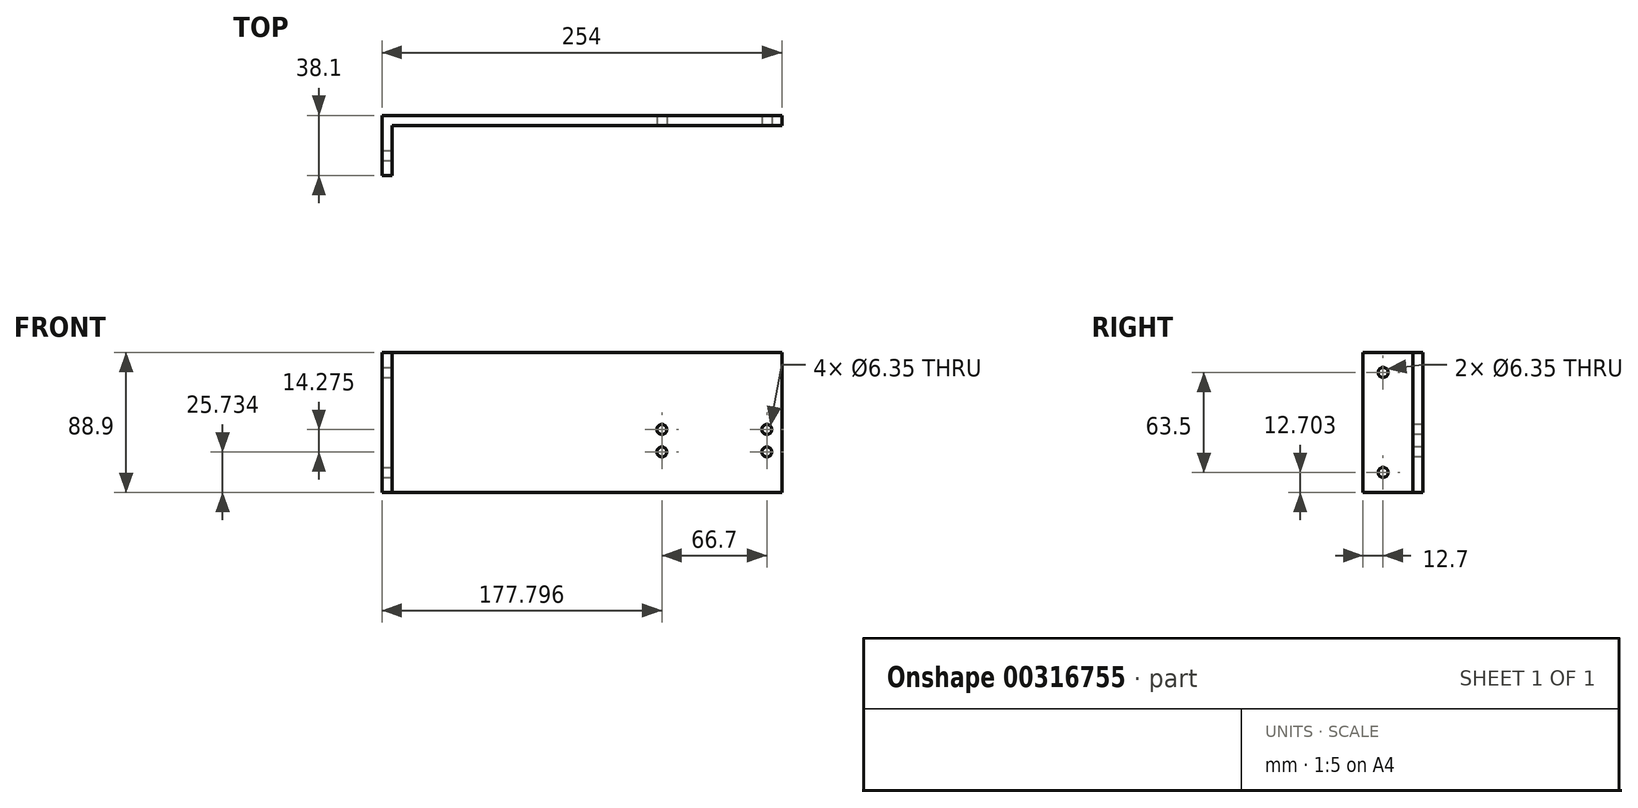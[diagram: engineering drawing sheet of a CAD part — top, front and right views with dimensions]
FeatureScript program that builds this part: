
annotation { "Feature Type Name" : "Feature", "Feature Type Description" : "" }
export const myFeature = defineFeature(function(context is Context, id is Id, definition is map)
    precondition{}
    {
        {
            var Q0;
            Q0=qCreatedBy(makeId("Front.planeOp"),FACE);
            var sketch = newSketch(context, id + "F0", { "sketchPlane" : qUnion([Q0])});
            skLineSegment(sketch, "E0.bottom", {"start": v(-29.12, 31.27) * mm, "end": v(224.88, 31.27) * mm});
            skLineSegment(sketch, "E0.top", {"start": v(-29.12, -57.63) * mm, "end": v(224.88, -57.63) * mm});
            skLineSegment(sketch, "E0.left", {"start": v(-29.12, 31.27) * mm, "end": v(-29.12, -57.63) * mm});
            skLineSegment(sketch, "E0.right", {"start": v(224.88, 31.27) * mm, "end": v(224.88, -57.63) * mm});
            skSolve(sketch);
        }
        {
            var Q0;
            Q0=makeQuery(id+"F0.imprint","IMPRINT",FACE,{"disambiguationData":[TD([[makeQuery(id+"F0.imprint","IMPRINT",EDGE,{"derivedFrom":sQuery(id+"F0.wireOp",EDGE,"E0.bottom")}),-1.0]])]});
            extrude(context, id + "F1", {"entities" : qUnion([Q0]), "depth" : 6.35 * mm});
        }
        {
            var Q0;
            Q0=makeQuery(id+"F1.opExtrude","CAP_FACE",FACE,{"disambiguationData":[OSD([sQuery(id+"F0.wireOp",EDGE,"E0.bottom"),sQuery(id+"F0.wireOp",EDGE,"E0.top"),sQuery(id+"F0.wireOp",EDGE,"E0.left"),sQuery(id+"F0.wireOp",EDGE,"E0.right")])],"isStart":false});
            var sketch = newSketch(context, id + "F2", { "sketchPlane" : qUnion([Q0])});
            skPoint(sketch, "E1", {"position": v(148.68, -31.9) * mm});
            skPoint(sketch, "E2", {"position": v(148.68, -17.62) * mm});
            skPoint(sketch, "E3", {"position": v(215.38, -17.62) * mm});
            skPoint(sketch, "E4", {"position": v(215.38, -31.9) * mm});
            skSolve(sketch);
        }
        {
            var Q0;
            Q0=sQuery(id+"F2.wireOp",VERTEX,"E2");
            var Q1;
            Q1=sQuery(id+"F2.wireOp",VERTEX,"E3");
            var Q2;
            Q2=sQuery(id+"F2.wireOp",VERTEX,"E4");
            var Q3;
            Q3=sQuery(id+"F2.wireOp",VERTEX,"E1");
            var Q4;
            Q4=makeQuery(id+"F1.opExtrude","SWEPT_BODY",BODY,{"disambiguationData":[OSD([sQuery(id+"F0.wireOp",EDGE,"E0.bottom"),sQuery(id+"F0.wireOp",EDGE,"E0.top"),sQuery(id+"F0.wireOp",EDGE,"E0.left"),sQuery(id+"F0.wireOp",EDGE,"E0.right")])]});
            hole(context, id + "F3", {"style" : HoleStyle.SIMPLE, "endStyle" : HoleEndStyle.THROUGH, "holeDiameter" : 6.35 * mm, "tappedDepth" : 12.7 * mm, "tapClearance" : 3, "locations" : qUnion([Q0, Q1, Q2, Q3]), "scope" : qUnion([Q4])});
        }
        {
            var Q0;
            Q0=makeQuery(id+"F1.opExtrude","CAP_FACE",FACE,{"disambiguationData":[OSD([sQuery(id+"F0.wireOp",EDGE,"E0.bottom"),sQuery(id+"F0.wireOp",EDGE,"E0.top"),sQuery(id+"F0.wireOp",EDGE,"E0.left"),sQuery(id+"F0.wireOp",EDGE,"E0.right")])],"isStart":false});
            var sketch = newSketch(context, id + "F4", { "sketchPlane" : qUnion([Q0])});
            skLineSegment(sketch, "E5.bottom", {"start": v(-29.12, 31.27) * mm, "end": v(-22.77, 31.27) * mm});
            skLineSegment(sketch, "E5.top", {"start": v(-29.12, -57.63) * mm, "end": v(-22.77, -57.63) * mm});
            skLineSegment(sketch, "E5.left", {"start": v(-29.12, 31.27) * mm, "end": v(-29.12, -57.63) * mm});
            skLineSegment(sketch, "E5.right", {"start": v(-22.77, 31.27) * mm, "end": v(-22.77, -57.63) * mm});
            skSolve(sketch);
        }
        {
            var Q0;
            Q0 = qSketchRegion(id + "F4", true);
            extrude(context, id + "F5", {"entities" : qUnion([Q0]), "operationType" : NewBodyOperationType.ADD, "depth" : 31.75 * mm});
        }
        {
            var Q0;
            Q0=makeQuery(id+"F5.opExtrude","SWEPT_FACE",FACE,{"disambiguationData":[OSD([sQuery(id+"F4.wireOp",EDGE,"E5.right")])]});
            var sketch = newSketch(context, id + "F6", { "sketchPlane" : qUnion([Q0])});
            skPoint(sketch, "E6", {"position": v(-25.4, -44.93) * mm});
            skPoint(sketch, "E7", {"position": v(-25.4, 18.57) * mm});
            skSolve(sketch);
        }
        {
            var Q0;
            Q0=sQuery(id+"F6.wireOp",VERTEX,"E6");
            var Q1;
            Q1=sQuery(id+"F6.wireOp",VERTEX,"E7");
            var Q2;
            Q2=makeQuery(id+"F1.opExtrude","SWEPT_BODY",BODY,{"disambiguationData":[OSD([sQuery(id+"F0.wireOp",EDGE,"E0.bottom"),sQuery(id+"F0.wireOp",EDGE,"E0.top"),sQuery(id+"F0.wireOp",EDGE,"E0.left"),sQuery(id+"F0.wireOp",EDGE,"E0.right")])]});
            hole(context, id + "F7", {"style" : HoleStyle.SIMPLE, "endStyle" : HoleEndStyle.THROUGH, "holeDiameter" : 6.35 * mm, "tappedDepth" : 12.7 * mm, "tapClearance" : 3, "locations" : qUnion([Q0, Q1]), "scope" : qUnion([Q2])});
        }
    });
